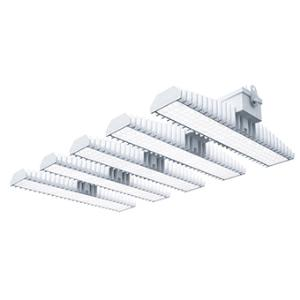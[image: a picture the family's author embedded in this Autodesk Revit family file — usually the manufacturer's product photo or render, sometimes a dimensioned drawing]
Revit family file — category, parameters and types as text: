
# Revit family: 3f_filippi_-_3f_lem_medio_3f_filippi_-_58915_a0812_-_3f_lem_5_led_250_dali_cr_medio___vs_952c
name_source: partatom
category: Lighting Fixtures
units: mm (PartAtom-declared; Revit-internal decimal feet)

## family parameters
Cut with Voids When Loaded = No
Host = Face
Light Source = No
Part Type = Normal
Room Calculation Point = No
Round Connector Dimension = Use Diameter
Shared = No

## types (1)
- 3F Filippi - 3F LEM Medio (1 x LED, 33664 lm, 274 W, 4000 K)
    Apparent Load = 274 VA
    Approval mark = CE
    CIE Flux Codes = 77 92 98 100 100
    Color Rendering = 80
    Color Temperature = 4000 K
    Control Gear = Electronic transformer
    Default Elevation = 1800 mm
    Description = Industrial luminaire with high light output and high luminous efficiency designed with the most innovative technologies for environments with temperature up to 55°C.

ILLUMINOTECHNICAL
Luminous efficiency 100% (DLOR 98%, ULOR 2%).
Initial luminous flux of the luminaire 33664 lm.
Medium distribution with rectangular shape.
Installation Interdistance Transv.D = 0.87 x hu - Long.D = 0.87 x hu.
Tabular UGR (CIE 117 - 4H-8H; S=0.25H; 70/50/20): RUG 21.2 - 21.2.
Beam angle: 58° - 57°.
Luminous efficacy 123 lm/W.
Lifetime (L93/B10): 30000 h. (tq+25°C)
Lifetime (L90/B10): 50000 h. (tq+25°C)
Lifetime (L85/B10): 80000 h. (tq+25°C)
Lifetime (L80/B10): 100000 h. (tq+25°C)
Lifetime (L85/B10): 50000 h. (tq+55°C)
Sudden decreased luminous flux after 50000 hours: 0% (C0).
Photobiological safety in compliance with IEC/TR 62778: RG0 risk exempt, (IEC 62471).
In compliance with IEC/EN 62722-2-1 - IEC/EN 62717 standards.

SOURCE
5 Mid-Power linear LED modules 50W/840.
Energy efficiency class (UE 2019/2020 - UE 2019/2015): C.
CIE 13.3 Colour rendering index: CRI >80 (R9 <50%).
IES TM-30 Fidelity Index: Rf = 84 Rg = 95.
CCT nominal colour temperature 4000 K.
Colour initial tolerance (MacAdam): SDCM 3.

MECHANICAL
Passive modular heatsinks in die-casted aluminium, painted in white colour.
To optimize the thermal management of the LED module, the heatsinks are oversized and provided with self-cleaning of cooling fins.
Wiring body in aluminium and galvanised steel anchored solidly to the sinks and thermally separated.
3F Lens lenses with high luminous efficiency, transparent methacrylate (PMMA), fixed to the LED modules.
Fixing brackets in stainless steel.
Luminaire with limited surface temperature. - D - (EN 60598-2-24)
Dimensions: 952x542 mm, height 133 mm. Weight 23.325 kg.
IP65 protection degree.
Mechanical strength to impacts IK06 (1 joule).
Glow-wire test resistance 650°C.

ELECTRICAL
Halogen Free DALI-2 DATI (Parts 251, 252, 253), PUSH-DIM, electronic wiring 230V-50/60Hz, power factor 0.97 at full load, THD <25%, constant output current, class I, 3 driver, 3 DALI addresses.
Power of the luminaire 274 W.
ENEC - CE.
SAFE FLICKER: PstLM=<1 and SVM=<0.4 (IEC TR 61547-1 and IEC TR 63158), to ensure a more comfortable and safe light.
Luminaire compliant with EN 60598-2-22 for power supply from a centralised emergency system CPSS (Central Power Supply System), not incorporated in the luminaire - high risk areas excluded. The default power and flux are 100% in AC and 15% in DC.
Ambient temperature from -30°C to +55°C.
Temperature class T6 max 85°C.
Quick connection via M25 5P connector with 9-13 mm tightening range.
Power unit positioned on a separate compartment by the LED module to ensure optimum temperatures of cabling components, to be inspectable and maintainable.
Relative humidity UR: <85%.

INSTALLATION
Ceiling / Suspended / Wall.
All accessories dedicated to this product are available on the Catalog and on our website www.3F-Filippi.com.

ACCESSORIES
A0812 - Anti-glare microprismatic VS moulded glass, tempered, not flammable, with sealing gasket.
One required for each light module. The pack contains 10 pieces.

APPLICATIONS
In commercial environments, exhibition and industrial areas, stores, open areas.
Applications with high ambient temperature up to 55°C.
Environments in which it is necessary a total protection against falling fragments (eg environments with foodstuffs or machines with moving parts or with extreme temperature changes), use luminaires with polycarbonate lenses.

LIGHT MANAGEMENT
Recommended minimum setting: 10%.
The luminaire, equipped with (DALI-2 DATI) driver, can be controlled manually with 3F Easy Dim technology or automatically/manually with wired or wireless DALI/D2D control systems.
The D2D driver guarantees interoperability with other devices with the same certification by making the following information available:
Device Data (Part 251), Energy Report (Part 252), Diagnosis & Maintenance (Part 253).
In electrical systems without a regulation system (manual or automatic) and DALI bus, a suitable jumper must be made on the DA-DA terminals of the appliance.

WARNING
Fixture not suitable for cold stores with an ambient temperature <0°C and/or relative humidity >85%.
Luminaire designed for disposal/recycling at end-of-life.
Replaceable (LED only) light source by a professional. Replaceable control gear by a professional.
    Height = 133 mm  [stored 0.436352 ft]
    Lamp = 1 x LED
    Lamp Light Flux = 33664 lm
    Lamp Power = 274 W
    Lamp count = 1
    Length = 952 mm
    Lifetime = 50000 h
    Luminous efficacy = 123 lm/W
    Manufacturer = 3F Filippi
    ModVariant = No
    Model = 3F Filippi - 58915+A0812 - 3F LEM 5 LED 250 DALI CR MEDIO + VS
    Mounting Place = Ceiling
    Mounting Type = Pendant
    Number of Poles = 1
    OnlyDefault = Yes
    Power Factor = 1
    Product Name = 3F Filippi - 3F LEM Medio
    Product group = pendant luminaire
    ProductGroupID = 9
    Protection Class = Protection class I
    Protection Degree = IP 65
    RLX_Detail_Level = 1
    RLX_Emergency_Light_Flux = 0 lm
    RLX_Emergency_Type = 0
    RLX_Emergency_Type_DB = No
    RlxData = <blob elided: 132165 chars, md5=02687c96>
    Socket = socket
    Standby Power = 0 W
    System Light Flux = 33664 lm
    System Power = 274 W
    Type Comments = Product without accessories
    Type Image = 3f_filippi_-_lem_5__a0812.jpg
    URL = http://relux.com
    VarID = ---
    Voltage = 0 V
    Weight = 0.00 kg
    Width = 542 mm

note: [stored X ft] marks values corroborated as IEEE doubles in the binary element streams (Revit-internal decimal feet)

## geometry (parser evidence)
native form markers: Blend x4, Sweep x14
no freeform markers — native parametric forms only
